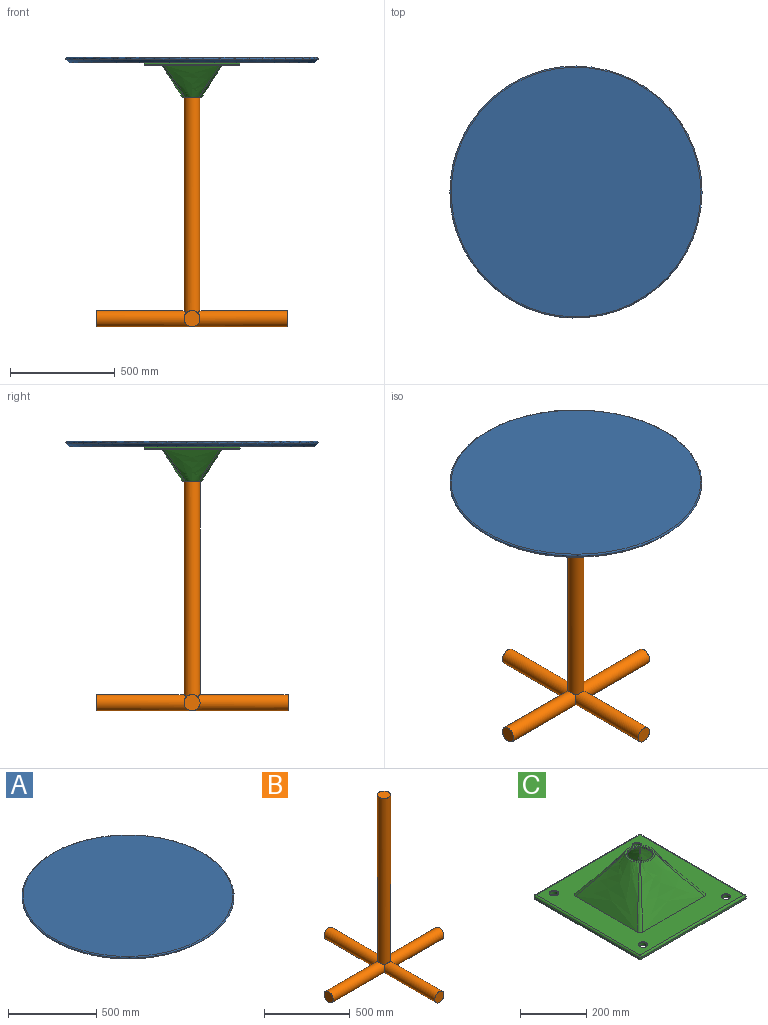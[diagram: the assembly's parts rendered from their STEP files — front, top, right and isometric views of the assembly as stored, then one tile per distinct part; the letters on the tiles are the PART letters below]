
ASSEMBLY  parts=3 mates=2
PART A: 12 faces, bbox 1300.2x1300.2x25.4 mm
  f0: plane 1188.54x1188.54mm, normal (0,0,1), area 1109474mm2, adj f3
  f1: plane 1168.4x1168.4mm, normal (0,0,-1), area 1070166.2mm2, adj f2,f4,f6,f8,f10
  f2: cone r=609.6mm half-angle=45deg, axis (0,0,1), area 76523.1mm2, adj f1,f3
  f3: torus R=594.27mm, axis (0,0,1), area 56298.6mm2, adj f0,f2
  f4: cylinder r=12.7mm len=25.4mm, axis (0,0,-1), area 1013.4mm2, adj f1,f5
  f5: plane 25.4x25.4mm, normal (0,0,-1), area 506.7mm2, adj f4
  f6: cylinder r=12.7mm len=25.4mm, axis (0,0,-1), area 1013.4mm2, adj f1,f7
  f7: plane 25.4x25.4mm, normal (0,0,-1), area 506.7mm2, adj f6
  f8: cylinder r=12.7mm len=25.4mm, axis (0,0,-1), area 1013.4mm2, adj f1,f9
  f9: plane 25.4x25.4mm, normal (0,0,-1), area 506.7mm2, adj f8
  f10: cylinder r=12.7mm len=25.4mm, axis (0,0,-1), area 1013.4mm2, adj f1,f11
  f11: plane 25.4x25.4mm, normal (0,0,-1), area 506.7mm2, adj f10
PART B: 10 faces, bbox 914.4x914.4x1257.3 mm
  f0: cylinder r=38.1mm len=457.2mm, axis (0,1,0), area 102439.8mm2, adj f1,f3,f4,f8
  f1: cylinder r=38.1mm len=457.2mm, axis (-1,0,0), area 102439.8mm2, adj f0,f2,f5,f8
  f2: cylinder r=38.1mm len=457.2mm, axis (0,1,0), area 102439.8mm2, adj f1,f3,f6,f8
  f3: cylinder r=38.1mm len=457.2mm, axis (-1,0,0), area 102439.8mm2, adj f0,f2,f7,f8
  f4: plane 76.2x76.2mm, normal (0,-1,0), area 4560.4mm2, adj f0
  f5: plane 76.2x76.2mm, normal (-1,0,0), area 4560.4mm2, adj f1
  f6: plane 76.2x76.2mm, normal (0,1,0), area 4560.4mm2, adj f2
  f7: plane 76.2x76.2mm, normal (1,0,0), area 4560.4mm2, adj f3
  f8: cylinder r=38.1mm len=1192.26mm, axis (0,0,-1), area 283652mm2, adj f0,f1,f2,f3,f9
  f9: plane 76.2x76.2mm, normal (0,0,1), area 4560.4mm2, adj f8
PART C: 54 faces, bbox 469.9x469.9x197.4 mm
  f0: plane 457.44x457.44mm, normal (0,0,-1), area 128058.5mm2, adj f21,f22,f23,f24,f25,f26,f27,f28
  f1: plane 449.01x449.01mm, normal (0,0,1), area 112330.1mm2, adj f2,f3,f4,f5,f7,f8,f9,f10
  f2: bspline ~304.8x165.1mm, area 31636.3mm2, adj f1,f6,f9,f10
  f3: bspline ~304.8x165.1mm, area 31636.3mm2, adj f1,f6,f8,f9
  f4: bspline ~304.8x165.1mm, area 31636.3mm2, adj f1,f6,f7,f8
  f5: bspline ~304.8x165.1mm, area 31636.3mm2, adj f1,f6,f7,f10
  f6: plane 91.45x91.45mm, normal (0,0,1), area 1618.9mm2, adj f2,f3,f4,f5,f49
  f7: bspline ~160.59x116.84mm, area 1406.2mm2, adj f1,f4,f5
  f8: bspline ~160.59x116.84mm, area 1406.2mm2, adj f1,f3,f4
  f9: bspline ~160.59x116.84mm, area 1406.2mm2, adj f1,f2,f3
  f10: bspline ~160.59x116.84mm, area 1406.2mm2, adj f1,f2,f5
  f11: offset ~317.5x177.8mm, area 31679.3mm2, adj f15,f18,f19,f25
  f12: offset ~317.5x177.8mm, area 31679.3mm2, adj f15,f17,f18,f27
  f13: offset ~317.5x177.8mm, area 31679.3mm2, adj f15,f16,f17,f21
  f14: offset ~317.5x177.8mm, area 31679.3mm2, adj f15,f16,f19,f23
  f15: plane 87.13x87.13mm, normal (0,0,-1), area 1140.7mm2, adj f11,f12,f13,f14,f16,f17,f18,f19
  f16: bspline ~180.11x129.42mm, area 1206.8mm2, adj f13,f14,f15,f22
  f17: bspline ~180.11x129.42mm, area 1206.8mm2, adj f12,f13,f15,f28
  f18: bspline ~180.11x129.42mm, area 1206.8mm2, adj f11,f12,f15,f26
  f19: bspline ~180.11x129.42mm, area 1206.8mm2, adj f11,f14,f15,f24
  f20: cylinder r=38.1mm len=76.2mm, axis (0,0,1), area 1140.1mm2, adj f15,f49
  f21: extruded ~269.89x6.35mm, area 1713.8mm2, adj f0,f13,f22,f28
  f22: extruded ~6.35x5.09mm, area 51.3mm2, adj f0,f16,f21,f23
  f23: extruded ~269.89x6.35mm, area 1713.8mm2, adj f0,f14,f22,f24
  f24: extruded ~6.35x5.09mm, area 51.3mm2, adj f0,f19,f23,f25
  f25: extruded ~269.89x6.35mm, area 1713.8mm2, adj f0,f11,f24,f26
  f26: extruded ~6.35x5.09mm, area 51.3mm2, adj f0,f18,f25,f27
  f27: extruded ~269.89x6.35mm, area 1713.8mm2, adj f0,f12,f26,f28
  f28: extruded ~6.35x5.09mm, area 51.3mm2, adj f0,f17,f21,f27
  f29: plane 444.5x6.35mm, normal (0,1,0), area 2822.6mm2, adj f0,f38,f42,f44
  f30: plane 444.5x6.35mm, normal (1,0,0), area 2822.6mm2, adj f0,f35,f41,f44
  f31: plane 444.5x6.35mm, normal (0,-1,0), area 2822.6mm2, adj f0,f33,f35,f36
  f32: plane 444.5x6.35mm, normal (-1,0,0), area 2822.6mm2, adj f0,f33,f37,f38
  f33: cylinder r=6.35mm len=6.35mm, axis (0,0,-1), area 63.3mm2, adj f0,f31,f32,f34
  f34: sphere r=6.35mm, area 40.3mm2, adj f33,f36,f37
  f35: cylinder r=6.35mm len=6.35mm, axis (0,0,1), area 63.3mm2, adj f0,f30,f31,f39
  f36: cylinder r=6.35mm len=444.5mm, axis (1,0,0), area 4433.7mm2, adj f1,f31,f34,f39
  f37: cylinder r=6.35mm len=444.5mm, axis (0,-1,0), area 4433.7mm2, adj f1,f32,f34,f40
  f38: cylinder r=6.35mm len=6.35mm, axis (0,0,1), area 63.3mm2, adj f0,f29,f32,f40
  f39: sphere r=6.35mm, area 63.3mm2, adj f35,f36,f41
  f40: sphere r=6.35mm, area 86.4mm2, adj f37,f38,f42
  f41: cylinder r=6.35mm len=444.5mm, axis (0,1,0), area 4433.7mm2, adj f1,f30,f39,f43
  f42: cylinder r=6.35mm len=444.5mm, axis (-1,0,0), area 4433.7mm2, adj f1,f29,f40,f43
  f43: sphere r=6.35mm, area 40.3mm2, adj f41,f42,f44
  f44: cylinder r=6.35mm len=6.35mm, axis (0,0,-1), area 63.3mm2, adj f0,f29,f30,f43
  f45: cylinder r=12.7mm len=25.4mm, axis (0,0,1), area 886.7mm2, adj f0,f50
  f46: cylinder r=12.7mm len=25.4mm, axis (0,0,1), area 886.7mm2, adj f0,f53
  f47: cylinder r=12.7mm len=25.4mm, axis (0,0,1), area 886.7mm2, adj f0,f52
  f48: cylinder r=12.7mm len=25.4mm, axis (0,0,1), area 886.7mm2, adj f0,f51
  f49: cone r=38.1mm half-angle=45deg, axis (0,0,1), area 548.6mm2, adj f6,f20
  f50: cone r=12.7mm half-angle=45deg, axis (0,0,1), area 190.3mm2, adj f1,f45
  f51: cone r=12.7mm half-angle=45deg, axis (0,0,1), area 190.3mm2, adj f1,f48
  f52: cone r=12.7mm half-angle=45deg, axis (0,0,1), area 190.3mm2, adj f1,f47
  f53: cone r=12.7mm half-angle=45deg, axis (0,0,1), area 190.3mm2, adj f1,f46
PLACE A t=(0,0,1219.2)mm
PLACE B at identity fixed
PLACE C rot(axis=(1,0,0),180deg) t=(0,0,1206.5)mm
MATE fastened C.f48 <-> A.f10  axis (0,0,1) through (-177.8,-190.5,1219.2)mm
MATE fastened B.f8 <-> A.f2  axis (0,0,1) through (0,0,1219.2)mm
